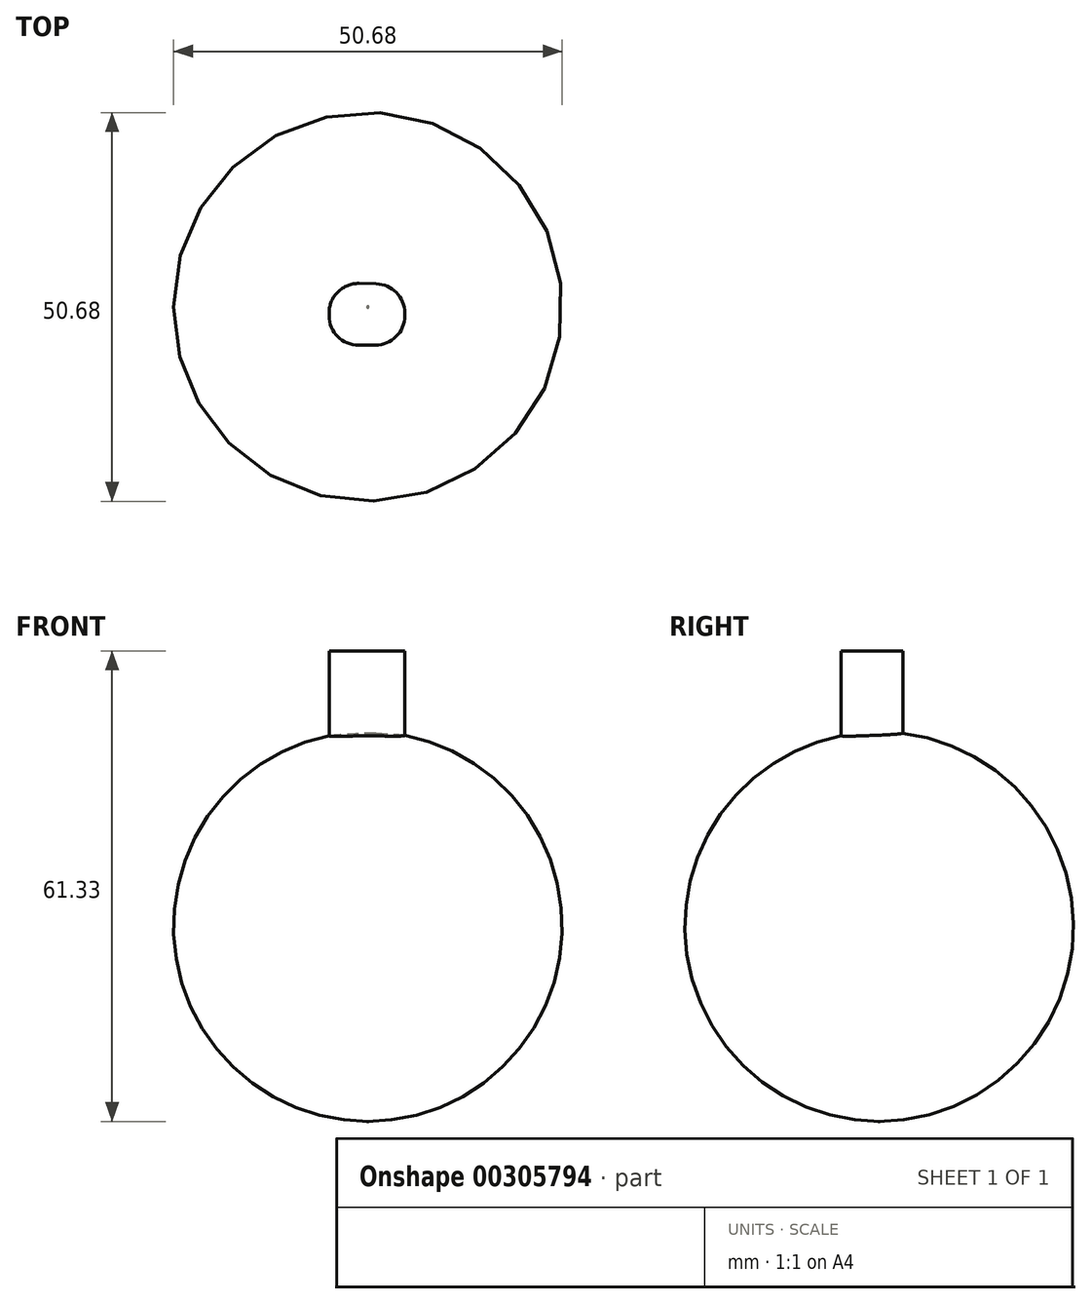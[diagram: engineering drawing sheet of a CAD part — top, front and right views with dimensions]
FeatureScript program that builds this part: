
annotation { "Feature Type Name" : "Feature", "Feature Type Description" : "" }
export const myFeature = defineFeature(function(context is Context, id is Id, definition is map)
    precondition{}
    {
        {
            var Q0;
            Q0=qCreatedBy(makeId("Front.planeOp"),FACE);
            var sketch = newSketch(context, id + "F0", { "sketchPlane" : qUnion([Q0])});
            skLineSegment(sketch, "E0", {"start": v(0, 27.57) * mm, "end": v(0, -23.23) * mm});
            skArc(sketch, "E1", {"start": v(0, 27.57) * mm, "mid": v(-25.34, 2.17) * mm, "end": v(0, -23.23) * mm});
            skSolve(sketch);
        }
        {
            var Q0;
            Q0=makeQuery(id+"F0.imprint","IMPRINT",FACE,{"disambiguationData":[TD([[makeQuery(id+"F0.imprint","IMPRINT",EDGE,{"derivedFrom":sQuery(id+"F0.wireOp",EDGE,"E0")}),-1.0]])]});
            var Q1;
            Q1=sQuery(id+"F0.wireOp",EDGE,"E0");
            revolve(context, id + "F1", {"entities" : qUnion([Q0]), "axis" : qUnion([Q1]), "revolveType" : RevolveType.ONE_DIRECTION, "angle" : 360 * degree});
        }
        {
            var Q0;
            Q0=qCreatedBy(makeId("Front.planeOp"),FACE);
            var sketch = newSketch(context, id + "F2", { "sketchPlane" : qUnion([Q0])});
            skLineSegment(sketch, "E2", {"start": v(-9.5, 18.4) * mm, "end": v(-14.58, 9.6) * mm});
            skLineSegment(sketch, "E3", {"start": v(-14.58, 9.6) * mm, "end": v(-4.42, 9.6) * mm});
            skLineSegment(sketch, "E4", {"start": v(-4.42, 9.6) * mm, "end": v(-9.5, 18.4) * mm});
            skSolve(sketch);
        }
        {
            var Q0;
            Q0 = qSketchRegion(id + "F2", true);
            var Q1;
            Q1 = qSketchRegion(id + "F4", true);
            var Q2;
            Q2=sQuery(id+"F2.wireOp",EDGE,"E3");
            var Q3;
            Q3=sQuery(id+"F2.wireOp",EDGE,"E2");
            var Q4;
            Q4=sQuery(id+"F2.wireOp",EDGE,"E4");
            extrude(context, id + "F3", {"entities" : qUnion([Q0, Q1]), "operationType" : NewBodyOperationType.REMOVE, "surfaceEntities" : qUnion([Q2, Q3, Q4]), "endBound" : BoundingType.THROUGH_ALL, "depth" : 25.4 * mm});
        }
        {
            var Q0;
            Q0=qCreatedBy(makeId("Top.planeOp"),FACE);
            var sketch = newSketch(context, id + "F4", { "sketchPlane" : qUnion([Q0])});
            skLineSegment(sketch, "E5", {"start": v(-5.05, 3.14) * mm, "end": v(-5.05, -4.98) * mm});
            skLineSegment(sketch, "E6", {"start": v(-5.05, -4.98) * mm, "end": v(4.8, -4.98) * mm});
            skLineSegment(sketch, "E7", {"start": v(4.8, -4.98) * mm, "end": v(4.8, 2.94) * mm});
            skLineSegment(sketch, "E8", {"start": v(-5.05, 3.14) * mm, "end": v(4.8, 2.94) * mm});
            skSolve(sketch);
        }
        {
            var Q0;
            Q0 = qSketchRegion(id + "F4", true);
            extrude(context, id + "F5", {"entities" : qUnion([Q0]), "operationType" : NewBodyOperationType.ADD, "depth" : 38.1 * mm});
        }
        {
            var Q0;
            Q0=qCreatedBy(makeId("Front.planeOp"),FACE);
            var sketch = newSketch(context, id + "F6", { "sketchPlane" : qUnion([Q0])});
            skLineSegment(sketch, "E9", {"start": v(8.26, 18.11) * mm, "end": v(3.18, 9.31) * mm});
            skLineSegment(sketch, "E10", {"start": v(3.18, 9.31) * mm, "end": v(13.34, 9.31) * mm});
            skLineSegment(sketch, "E11", {"start": v(13.34, 9.31) * mm, "end": v(8.26, 18.11) * mm});
            skSolve(sketch);
        }
        {
            var Q0;
            Q0 = qSketchRegion(id + "F6", true);
            var Q1;
            Q1=sQuery(id+"F6.wireOp",EDGE,"E11");
            var Q2;
            Q2=sQuery(id+"F6.wireOp",EDGE,"E9");
            var Q3;
            Q3=sQuery(id+"F6.wireOp",EDGE,"E10");
            extrude(context, id + "F7", {"entities" : qUnion([Q0]), "operationType" : NewBodyOperationType.REMOVE, "surfaceEntities" : qUnion([Q1, Q2, Q3]), "depth" : 25.4 * mm});
        }
        {
            var Q0;
            Q0=qCreatedBy(makeId("Front.planeOp"),FACE);
            var sketch = newSketch(context, id + "F8", { "sketchPlane" : qUnion([Q0])});
            skCircle(sketch, "E12", {"center": v(-2.87, 1.86) * mm, "radius": 1.17 * mm});
            skCircle(sketch, "E13", {"center": v(3, 1.86) * mm, "radius": 1.17 * mm});
            skSolve(sketch);
        }
        {
            var Q0;
            Q0 = qSketchRegion(id + "F8", true);
            var Q1;
            Q1=sQuery(id+"F8.wireOp",EDGE,"E12");
            var Q2;
            Q2=sQuery(id+"F8.wireOp",EDGE,"E13");
            extrude(context, id + "F9", {"entities" : qUnion([Q0]), "operationType" : NewBodyOperationType.REMOVE, "surfaceEntities" : qUnion([Q1, Q2]), "endBound" : BoundingType.THROUGH_ALL, "depth" : 25.4 * mm});
        }
        {
            var Q0;
            Q0=qCreatedBy(makeId("Front.planeOp"),FACE);
            var sketch = newSketch(context, id + "F10", { "sketchPlane" : qUnion([Q0])});
            skArc(sketch, "E14", {"start": v(-22.5, 0.81) * mm, "mid": v(-16.82, -1.93) * mm, "end": v(-10.81, -3.86) * mm});
            skArc(sketch, "E15", {"start": v(-22.5, 0.81) * mm, "mid": v(-0.3, -15.15) * mm, "end": v(22.06, 0.62) * mm});
            skPoint(sketch, "E16.startSnap0", {"position": v(-0.25, -5.16) * mm});
            skLineSegment(sketch, "E17", {"start": v(-10.81, -3.86) * mm, "end": v(-10.81, -3.86) * mm});
            skFitSpline(sketch, "E18", {"points": [v(4.61, -4.92) * mm, v(5.1, -10.48) * mm, v(9.2, -4.2) * mm], "startDerivative": vector(-0.46, -17.55) * mm, "endDerivative": vector(9.4, 18.14) * mm});
            skFitSpline(sketch, "E19", {"points": [v(-10.81, -3.86) * mm, v(-8.28, -10.63) * mm, v(-7.4, -4.56) * mm], "startDerivative": vector(5.62, -19.74) * mm, "endDerivative": vector(1.14, 18.85) * mm});
            skArc(sketch, "E20", {"start": v(-7.4, -4.56) * mm, "mid": v(-1.4, -5.14) * mm, "end": v(4.61, -4.92) * mm});
            skArc(sketch, "E21", {"start": v(9.2, -4.2) * mm, "mid": v(15.82, -2.29) * mm, "end": v(22.06, 0.62) * mm});
            skSolve(sketch);
        }
        {
            var Q0;
            Q0 = qSketchRegion(id + "F10", true);
            var Q1;
            Q1=sQuery(id+"F10.wireOp",EDGE,"E14");
            var Q2;
            Q2=sQuery(id+"F10.wireOp",EDGE,"E15");
            var Q3;
            Q3=sQuery(id+"F10.wireOp",EDGE,"E19");
            var Q4;
            Q4=sQuery(id+"F10.wireOp",EDGE,"E20");
            var Q5;
            Q5=sQuery(id+"F10.wireOp",EDGE,"E18");
            var Q6;
            Q6=sQuery(id+"F10.wireOp",EDGE,"E21");
            extrude(context, id + "F11", {"entities" : qUnion([Q0]), "operationType" : NewBodyOperationType.REMOVE, "surfaceEntities" : qUnion([Q1, Q2, Q3, Q4, Q5, Q6]), "depth" : 25.4 * mm});
        }
        {
            var Q0;
            Q0=makeQuery(id+"F5.opExtrude","SWEPT_EDGE",EDGE,{"disambiguationData":[OSD([sQuery(id+"F4.wireOp",EDGE,"E7"),sQuery(id+"F4.wireOp",EDGE,"E8")])]});
            var Q1;
            Q1=makeQuery(id+"F5.opExtrude","SWEPT_EDGE",EDGE,{"disambiguationData":[OSD([sQuery(id+"F4.wireOp",EDGE,"E5"),sQuery(id+"F4.wireOp",EDGE,"E8")])]});
            var Q2;
            {var subQ0=sQuery(id+"F4.wireOp",EDGE,"E6");var subQ1=sQuery(id+"F4.wireOp",EDGE,"E5");Q2=makeQuery(id+"F5.boolean.opBoolean","SPLIT",EDGE,{"disambiguationData":[TD([makeQuery(id+"F1.opRevolve","SWEPT_FACE",FACE,{"disambiguationData":[OSD([sQuery(id+"F0.wireOp",EDGE,"E1")])]})])],"derivedFrom":makeQuery(id+"F5.opExtrude","SWEPT_EDGE",EDGE,{"disambiguationData":[OSD([subQ1,subQ0])]})});}
            var Q3;
            Q3=makeQuery(id+"F5.opExtrude","SWEPT_EDGE",EDGE,{"disambiguationData":[OSD([sQuery(id+"F4.wireOp",EDGE,"E6"),sQuery(id+"F4.wireOp",EDGE,"E7")])]});
            fillet(context, id + "F12", {"entities" : qUnion([Q0, Q1, Q2, Q3]), "radius" : 3.8 * mm, "tangentPropagation" : true, "allowEdgeOverflow" : false});
        }
    });
